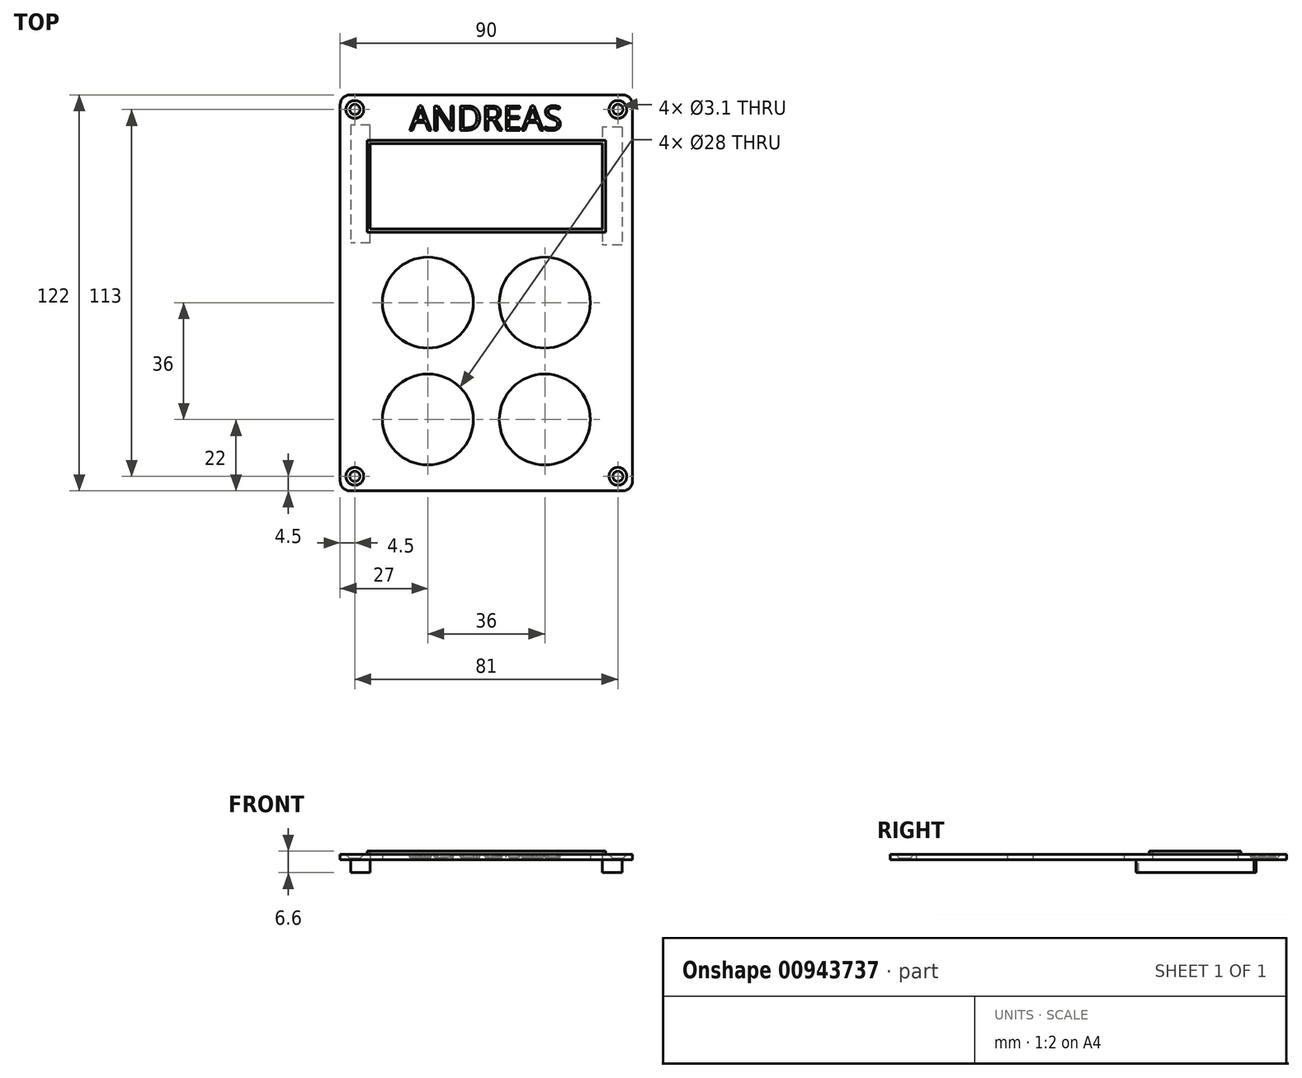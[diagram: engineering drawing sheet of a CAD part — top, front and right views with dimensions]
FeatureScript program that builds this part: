
annotation { "Feature Type Name" : "Feature", "Feature Type Description" : "" }
export const myFeature = defineFeature(function(context is Context, id is Id, definition is map)
    precondition{}
    {
        {
            var Q0;
            Q0=qCreatedBy(makeId("Top.planeOp"),FACE);
            var sketch = newSketch(context, id + "F0", { "sketchPlane" : qUnion([Q0])});
            skLineSegment(sketch, "E0.bottom", {"start": v(42, -93.85) * mm, "end": v(-42, -93.85) * mm});
            skLineSegment(sketch, "E0.top", {"start": v(42, 28.15) * mm, "end": v(-42, 28.15) * mm});
            skLineSegment(sketch, "E0.left", {"start": v(45, -90.85) * mm, "end": v(45, 25.15) * mm});
            skLineSegment(sketch, "E0.right", {"start": v(-45, -90.85) * mm, "end": v(-45, 25.15) * mm});
            skCircle(sketch, "E1", {"center": v(-40.5, -89.35) * mm, "radius": 1.55 * mm});
            skCircle(sketch, "E2", {"center": v(40.5, 23.65) * mm, "radius": 1.55 * mm});
            skCircle(sketch, "E3", {"center": v(40.5, -89.35) * mm, "radius": 1.55 * mm});
            skLineSegment(sketch, "E4.bottom", {"start": v(35.75, -13.15) * mm, "end": v(-35.75, -13.15) * mm});
            skLineSegment(sketch, "E4.top", {"start": v(35.75, 13.15) * mm, "end": v(-35.75, 13.15) * mm});
            skLineSegment(sketch, "E4.left", {"start": v(35.75, -13.15) * mm, "end": v(35.75, 13.15) * mm});
            skLineSegment(sketch, "E4.right", {"start": v(-35.75, -13.15) * mm, "end": v(-35.75, 13.15) * mm});
            skPoint(sketch, "E4.middle", {"position": v(0, 0) * mm});
            skPoint(sketch, "E5", {"position": v(0, 28.15) * mm});
            skCircle(sketch, "E6", {"center": v(-18, -35.85) * mm, "radius": 14 * mm});
            skCircle(sketch, "E7", {"center": v(18, -35.85) * mm, "radius": 14 * mm});
            skCircle(sketch, "E8", {"center": v(-18, -71.85) * mm, "radius": 14 * mm});
            skCircle(sketch, "E9", {"center": v(18, -71.85) * mm, "radius": 14 * mm});
            skPoint(sketch, "E10.visualSharp", {"position": v(45, 28.15) * mm});
            skArc(sketch, "E10.filletArc", {"start": v(45, 25.15) * mm, "mid": v(44.12, 27.27) * mm, "end": v(42, 28.15) * mm});
            skPoint(sketch, "E11.visualSharp", {"position": v(-45, 28.15) * mm});
            skArc(sketch, "E11.filletArc", {"start": v(-42, 28.15) * mm, "mid": v(-44.12, 27.27) * mm, "end": v(-45, 25.15) * mm});
            skPoint(sketch, "E12.visualSharp", {"position": v(-45, -93.85) * mm});
            skArc(sketch, "E12.filletArc", {"start": v(-45, -90.85) * mm, "mid": v(-44.12, -92.97) * mm, "end": v(-42, -93.85) * mm});
            skPoint(sketch, "E13.visualSharp", {"position": v(45, -93.85) * mm});
            skArc(sketch, "E13.filletArc", {"start": v(42, -93.85) * mm, "mid": v(44.12, -92.97) * mm, "end": v(45, -90.85) * mm});
            skCircle(sketch, "E14", {"center": v(-40.5, 23.65) * mm, "radius": 1.55 * mm});
            skSolve(sketch);
        }
        {
            var Q0;
            Q0 = qSketchRegion(id + "F0", true);
            var Q1;
            Q1 = qSketchRegion(id + "F2", true);
            extrude(context, id + "F1", {"entities" : qUnion([Q0, Q1]), "depth" : 1.6 * mm, "offsetDistance" : 25 * mm});
        }
        {
            var Q0;
            Q0=makeQuery(id+"F1.opExtrude","CAP_FACE",FACE,{"disambiguationData":[OSD([sQuery(id+"F0.wireOp",EDGE,"E0.bottom"),sQuery(id+"F0.wireOp",EDGE,"E0.top"),sQuery(id+"F0.wireOp",EDGE,"E0.left"),sQuery(id+"F0.wireOp",EDGE,"E0.right"),sQuery(id+"F0.wireOp",EDGE,"E1"),sQuery(id+"F0.wireOp",EDGE,"16f8IFU0-oIQh-cnNS-k59y-e92YAkWsYWvI"),sQuery(id+"F0.wireOp",EDGE,"E2"),sQuery(id+"F0.wireOp",EDGE,"E3"),sQuery(id+"F0.wireOp",EDGE,"E4.bottom"),sQuery(id+"F0.wireOp",EDGE,"E4.top"),sQuery(id+"F0.wireOp",EDGE,"E4.left"),sQuery(id+"F0.wireOp",EDGE,"E4.right"),sQuery(id+"F0.wireOp",EDGE,"E6"),sQuery(id+"F0.wireOp",EDGE,"E7"),sQuery(id+"F0.wireOp",EDGE,"E8"),sQuery(id+"F0.wireOp",EDGE,"E9"),sQuery(id+"F0.wireOp",EDGE,"E10.filletArc"),sQuery(id+"F0.wireOp",EDGE,"E11.filletArc"),sQuery(id+"F0.wireOp",EDGE,"E12.filletArc"),sQuery(id+"F0.wireOp",EDGE,"E13.filletArc")])],"isStart":false});
            var sketch = newSketch(context, id + "F2", { "sketchPlane" : qUnion([Q0])});
            skText(sketch, "E15", { "text": "ANDREAS", "fontName": "OpenSans-Regular.ttf"});
            const initialGuessF2  = {"E15": [-0.02359, 0.01725, 1, 0, 0.00755]};
            skSetInitialGuess(sketch, initialGuessF2);
            skSolve(sketch);
        }
        {
            var Q0;
            Q0=makeQuery(id+"F2.imprint","IMPRINT",FACE,{"disambiguationData":[TD([[makeQuery(id+"F2.imprint","IMPRINT",EDGE,{"derivedFrom":sQuery(id+"F2.wireOp",EDGE,"E15.sketch_text.stroke-0")}),-1.0]])]});
            var Q1;
            Q1=makeQuery(id+"F2.imprint","IMPRINT",FACE,{"disambiguationData":[TD([[makeQuery(id+"F2.imprint","IMPRINT",EDGE,{"derivedFrom":sQuery(id+"F2.wireOp",EDGE,"E15.sketch_text.stroke-13")}),-1.0]])]});
            var Q2;
            Q2=makeQuery(id+"F2.imprint","IMPRINT",FACE,{"disambiguationData":[TD([[makeQuery(id+"F2.imprint","IMPRINT",EDGE,{"derivedFrom":sQuery(id+"F2.wireOp",EDGE,"E15.sketch_text.stroke-28")}),-1.0]])]});
            var Q3;
            Q3=makeQuery(id+"F2.imprint","IMPRINT",FACE,{"disambiguationData":[TD([[makeQuery(id+"F2.imprint","IMPRINT",EDGE,{"derivedFrom":sQuery(id+"F2.wireOp",EDGE,"E15.sketch_text.stroke-42")}),-1.0]])]});
            var Q4;
            Q4=makeQuery(id+"F2.imprint","IMPRINT",FACE,{"disambiguationData":[TD([[makeQuery(id+"F2.imprint","IMPRINT",EDGE,{"derivedFrom":sQuery(id+"F2.wireOp",EDGE,"E15.sketch_text.stroke-60")}),-1.0]])]});
            var Q5;
            Q5=makeQuery(id+"F2.imprint","IMPRINT",FACE,{"disambiguationData":[TD([[makeQuery(id+"F2.imprint","IMPRINT",EDGE,{"derivedFrom":sQuery(id+"F2.wireOp",EDGE,"E15.sketch_text.stroke-72")}),-1.0]])]});
            var Q6;
            Q6=makeQuery(id+"F2.imprint","IMPRINT",FACE,{"disambiguationData":[TD([[makeQuery(id+"F2.imprint","IMPRINT",EDGE,{"derivedFrom":sQuery(id+"F2.wireOp",EDGE,"E15.sketch_text.stroke-85")}),-1.0]])]});
            extrude(context, id + "F3", {"entities" : qUnion([Q0, Q1, Q2, Q3, Q4, Q5, Q6]), "operationType" : NewBodyOperationType.REMOVE, "depth" : -0.8 * mm, "offsetDistance" : 25 * mm});
        }
        {
            var Q0;
            {var subQ0=sQuery(id+"F0.wireOp",EDGE,"E12.filletArc");var subQ1=sQuery(id+"F0.wireOp",EDGE,"E11.filletArc");var subQ2=sQuery(id+"F0.wireOp",EDGE,"E9");var subQ3=sQuery(id+"F0.wireOp",EDGE,"E8");var subQ4=sQuery(id+"F0.wireOp",EDGE,"E7");var subQ5=sQuery(id+"F0.wireOp",EDGE,"E6");var subQ6=sQuery(id+"F0.wireOp",EDGE,"E4.right");var subQ7=sQuery(id+"F0.wireOp",EDGE,"E4.left");var subQ8=sQuery(id+"F0.wireOp",EDGE,"E10.filletArc");var subQ9=sQuery(id+"F0.wireOp",EDGE,"E0.left");var subQ10=sQuery(id+"F0.wireOp",EDGE,"E0.top");var subQ11=sQuery(id+"F0.wireOp",EDGE,"E0.right");var subQ12=sQuery(id+"F0.wireOp",EDGE,"E0.bottom");var subQ13=sQuery(id+"F0.wireOp",EDGE,"E4.top");var subQ14=sQuery(id+"F0.wireOp",EDGE,"E1");var subQ15=sQuery(id+"F0.wireOp",EDGE,"E13.filletArc");var subQ16=sQuery(id+"F0.wireOp",EDGE,"16f8IFU0-oIQh-cnNS-k59y-e92YAkWsYWvI");var subQ17=sQuery(id+"F0.wireOp",EDGE,"E2");var subQ18=sQuery(id+"F0.wireOp",EDGE,"E3");var subQ19=sQuery(id+"F0.wireOp",EDGE,"E4.bottom");Q0=makeQuery(id+"F3.boolean.opBoolean","SPLIT",FACE,{"disambiguationData":[TD([makeQuery(id+"F1.opExtrude","SWEPT_FACE",FACE,{"disambiguationData":[OSD([subQ12])]})])],"derivedFrom":makeQuery(id+"F1.opExtrude","CAP_FACE",FACE,{"disambiguationData":[OSD([subQ12,subQ10,subQ9,subQ11,subQ14,subQ16,subQ17,subQ18,subQ19,subQ13,subQ7,subQ6,subQ5,subQ4,subQ3,subQ2,subQ8,subQ1,subQ0,subQ15])],"isStart":false})});}
            var sketch = newSketch(context, id + "F4", { "sketchPlane" : qUnion([Q0])});
            skLineSegment(sketch, "E16.0", {"start": v(36.75, 14.15) * mm, "end": v(-36.75, 14.15) * mm});
            skLineSegment(sketch, "E16.1", {"start": v(36.75, -14.15) * mm, "end": v(36.75, 14.15) * mm});
            skLineSegment(sketch, "E16.2", {"start": v(36.75, -14.15) * mm, "end": v(-36.75, -14.15) * mm});
            skLineSegment(sketch, "E16.3", {"start": v(-36.75, -14.15) * mm, "end": v(-36.75, 14.15) * mm});
            skSolve(sketch);
        }
        {
            var Q0;
            Q0=makeQuery(id+"F4.imprint","IMPRINT",FACE,{"disambiguationData":[TD([[makeQuery(id+"F4.imprint","IMPRINT",EDGE,{"derivedFrom":sQuery(id+"F4.wireOp",EDGE,"E16.0")}),1.0]])]});
            extrude(context, id + "F5", {"entities" : qUnion([Q0]), "operationType" : NewBodyOperationType.ADD, "depth" : 1 * mm, "offsetDistance" : 25 * mm});
        }
        {
            var Q0;
            Q0=makeQuery(id+"F1.opExtrude","CAP_FACE",FACE,{"disambiguationData":[OSD([sQuery(id+"F0.wireOp",EDGE,"E0.bottom"),sQuery(id+"F0.wireOp",EDGE,"E0.top"),sQuery(id+"F0.wireOp",EDGE,"E0.left"),sQuery(id+"F0.wireOp",EDGE,"E0.right"),sQuery(id+"F0.wireOp",EDGE,"E1"),sQuery(id+"F0.wireOp",EDGE,"16f8IFU0-oIQh-cnNS-k59y-e92YAkWsYWvI"),sQuery(id+"F0.wireOp",EDGE,"E2"),sQuery(id+"F0.wireOp",EDGE,"E3"),sQuery(id+"F0.wireOp",EDGE,"E4.bottom"),sQuery(id+"F0.wireOp",EDGE,"E4.top"),sQuery(id+"F0.wireOp",EDGE,"E4.left"),sQuery(id+"F0.wireOp",EDGE,"E4.right"),sQuery(id+"F0.wireOp",EDGE,"E6"),sQuery(id+"F0.wireOp",EDGE,"E7"),sQuery(id+"F0.wireOp",EDGE,"E8"),sQuery(id+"F0.wireOp",EDGE,"E9"),sQuery(id+"F0.wireOp",EDGE,"E10.filletArc"),sQuery(id+"F0.wireOp",EDGE,"E11.filletArc"),sQuery(id+"F0.wireOp",EDGE,"E12.filletArc"),sQuery(id+"F0.wireOp",EDGE,"E13.filletArc")])],"isStart":true});
            var sketch = newSketch(context, id + "F6", { "sketchPlane" : qUnion([Q0])});
            skLineSegment(sketch, "E17.bottom", {"start": v(41.75, -18.15) * mm, "end": v(35.75, -18.15) * mm});
            skLineSegment(sketch, "E17.top", {"start": v(41.75, 18.15) * mm, "end": v(35.75, 18.15) * mm});
            skLineSegment(sketch, "E17.left", {"start": v(41.75, -18.15) * mm, "end": v(41.75, 18.15) * mm});
            skLineSegment(sketch, "E17.right", {"start": v(35.75, -18.15) * mm, "end": v(35.75, 18.15) * mm});
            skLineSegment(sketch, "E18.bottom", {"start": v(-35.75, -18.85) * mm, "end": v(-41.75, -18.85) * mm});
            skLineSegment(sketch, "E18.top", {"start": v(-35.75, 17.45) * mm, "end": v(-41.75, 17.45) * mm});
            skLineSegment(sketch, "E18.left", {"start": v(-35.75, -18.85) * mm, "end": v(-35.75, 17.45) * mm});
            skLineSegment(sketch, "E18.right", {"start": v(-41.75, -18.85) * mm, "end": v(-41.75, 17.45) * mm});
            skSolve(sketch);
        }
        {
            var Q0;
            {var subQ2=sQuery(id+"F6.wireOp",EDGE,"E17.bottom");Q0=makeQuery(id+"F6.imprint","IMPRINT",FACE,{"disambiguationData":[TD([[makeQuery(id+"F6.imprint","IMPRINT",EDGE,{"derivedFrom":subQ2}),-1.0]])]});}
            var Q1;
            {var subQ3=sQuery(id+"F6.wireOp",EDGE,"E18.bottom");Q1=makeQuery(id+"F6.imprint","IMPRINT",FACE,{"disambiguationData":[TD([[makeQuery(id+"F6.imprint","IMPRINT",EDGE,{"derivedFrom":subQ3}),-1.0]])]});}
            extrude(context, id + "F7", {"entities" : qUnion([Q0, Q1]), "operationType" : NewBodyOperationType.ADD, "depth" : 4 * mm, "offsetDistance" : 25 * mm});
        }
        {
            var Q0;
            {var subQ0=sQuery(id+"F0.wireOp",EDGE,"E13.filletArc");var subQ1=sQuery(id+"F0.wireOp",EDGE,"E12.filletArc");var subQ2=sQuery(id+"F0.wireOp",EDGE,"E10.filletArc");var subQ3=sQuery(id+"F0.wireOp",EDGE,"E9");var subQ4=sQuery(id+"F0.wireOp",EDGE,"E8");var subQ5=sQuery(id+"F0.wireOp",EDGE,"E7");var subQ6=sQuery(id+"F0.wireOp",EDGE,"E6");var subQ7=sQuery(id+"F0.wireOp",EDGE,"E4.right");var subQ8=sQuery(id+"F0.wireOp",EDGE,"E11.filletArc");var subQ9=sQuery(id+"F0.wireOp",EDGE,"E0.left");var subQ10=sQuery(id+"F0.wireOp",EDGE,"E0.top");var subQ11=sQuery(id+"F0.wireOp",EDGE,"E0.right");var subQ12=sQuery(id+"F0.wireOp",EDGE,"E0.bottom");var subQ13=sQuery(id+"F0.wireOp",EDGE,"E4.left");var subQ14=sQuery(id+"F0.wireOp",EDGE,"E1");var subQ15=sQuery(id+"F0.wireOp",EDGE,"E14");var subQ16=sQuery(id+"F0.wireOp",EDGE,"E2");var subQ17=sQuery(id+"F0.wireOp",EDGE,"E3");var subQ18=sQuery(id+"F0.wireOp",EDGE,"E4.bottom");var subQ19=sQuery(id+"F0.wireOp",EDGE,"E4.top");Q0=makeQuery(id+"F3.boolean.opBoolean","SPLIT",FACE,{"disambiguationData":[TD([makeQuery(id+"F1.opExtrude","SWEPT_FACE",FACE,{"disambiguationData":[OSD([subQ12])]})])],"derivedFrom":makeQuery(id+"F1.opExtrude","CAP_FACE",FACE,{"disambiguationData":[OSD([subQ12,subQ10,subQ9,subQ11,subQ14,subQ16,subQ17,subQ18,subQ19,subQ13,subQ7,subQ6,subQ5,subQ4,subQ3,subQ2,subQ8,subQ1,subQ0,subQ15])],"isStart":false})});}
            var sketch = newSketch(context, id + "F8", { "sketchPlane" : qUnion([Q0])});
            skPoint(sketch, "E19", {"position": v(-40.5, 23.65) * mm});
            skPoint(sketch, "E20", {"position": v(40.5, 23.65) * mm});
            skPoint(sketch, "E21", {"position": v(40.5, -89.35) * mm});
            skPoint(sketch, "E22", {"position": v(-40.5, -89.35) * mm});
            skSolve(sketch);
        }
        {
            var Q0;
            Q0=sQuery(id+"F8.wireOp",VERTEX,"E19");
            var Q1;
            Q1=sQuery(id+"F8.wireOp",VERTEX,"E20");
            var Q2;
            Q2=sQuery(id+"F8.wireOp",VERTEX,"E22");
            var Q3;
            Q3=sQuery(id+"F8.wireOp",VERTEX,"E21");
            var Q4;
            Q4=makeQuery(id+"F1.opExtrude","SWEPT_BODY",BODY,{"disambiguationData":[OSD([sQuery(id+"F0.wireOp",EDGE,"E0.bottom"),sQuery(id+"F0.wireOp",EDGE,"E0.top"),sQuery(id+"F0.wireOp",EDGE,"E0.left"),sQuery(id+"F0.wireOp",EDGE,"E0.right"),sQuery(id+"F0.wireOp",EDGE,"E1"),sQuery(id+"F0.wireOp",EDGE,"E2"),sQuery(id+"F0.wireOp",EDGE,"E3"),sQuery(id+"F0.wireOp",EDGE,"E4.bottom"),sQuery(id+"F0.wireOp",EDGE,"E4.top"),sQuery(id+"F0.wireOp",EDGE,"E4.left"),sQuery(id+"F0.wireOp",EDGE,"E4.right"),sQuery(id+"F0.wireOp",EDGE,"E6"),sQuery(id+"F0.wireOp",EDGE,"E7"),sQuery(id+"F0.wireOp",EDGE,"E8"),sQuery(id+"F0.wireOp",EDGE,"E9"),sQuery(id+"F0.wireOp",EDGE,"E10.filletArc"),sQuery(id+"F0.wireOp",EDGE,"E11.filletArc"),sQuery(id+"F0.wireOp",EDGE,"E12.filletArc"),sQuery(id+"F0.wireOp",EDGE,"E13.filletArc"),sQuery(id+"F0.wireOp",EDGE,"E14")])]});
            hole(context, id + "F9", {"style" : HoleStyle.C_SINK, "endStyle" : HoleEndStyle.THROUGH, "holeDiameter" : 3.1 * mm, "cSinkDiameter" : 5.5 * mm, "cSinkAngle" : 90 * degree, "majorDiameter" : 5 * mm, "isTappedThrough" : true, "tappedDepth" : 12 * mm, "tapClearance" : 3, "locations" : qUnion([Q0, Q1, Q2, Q3]), "scope" : qUnion([Q4])});
        }
    });
